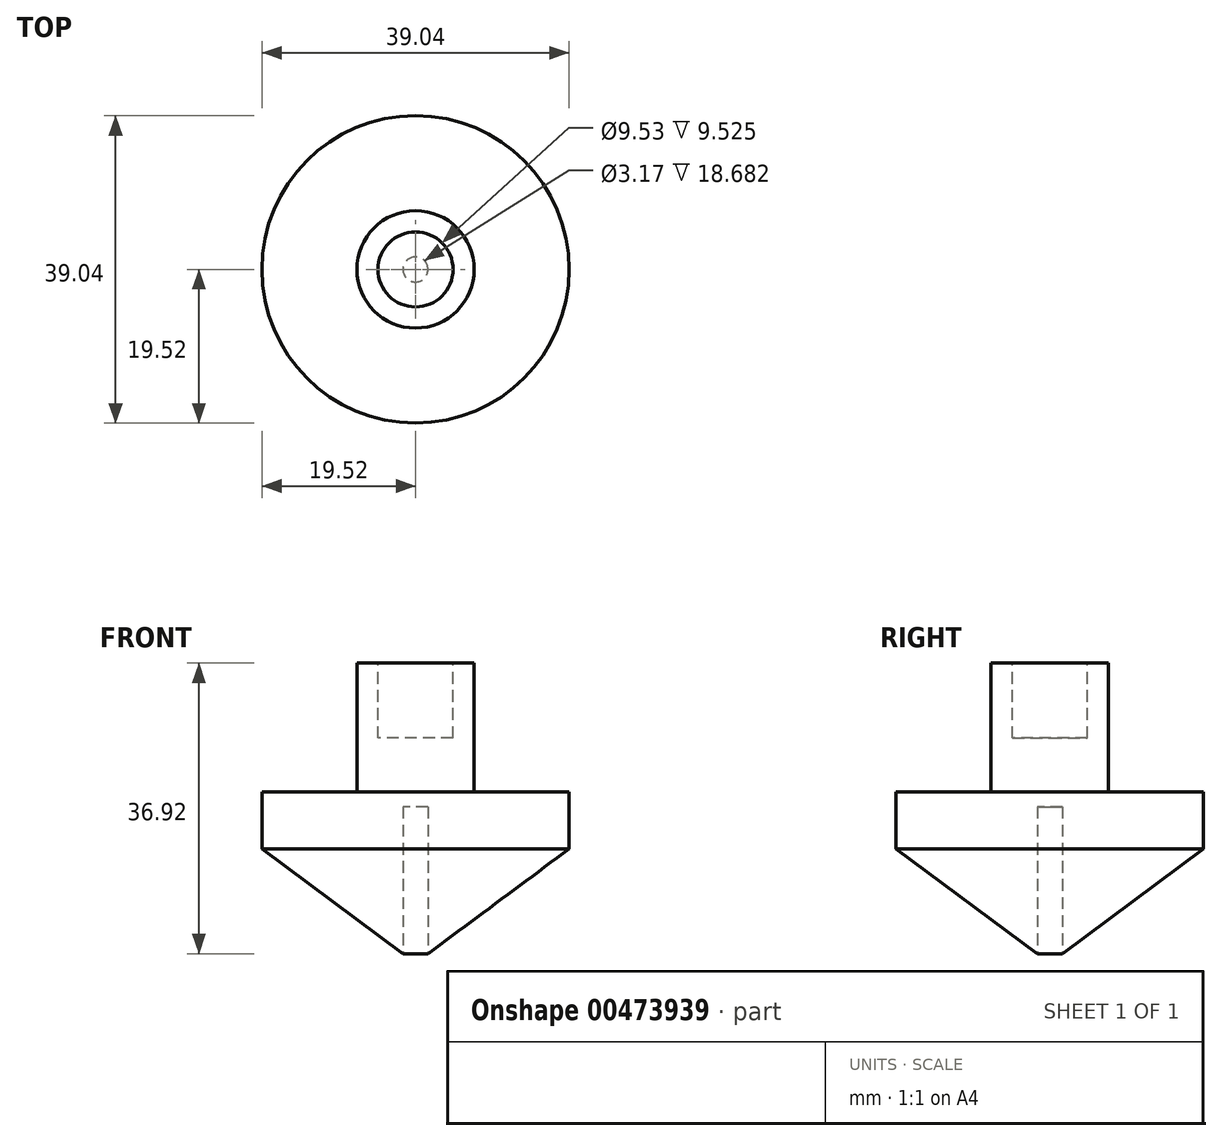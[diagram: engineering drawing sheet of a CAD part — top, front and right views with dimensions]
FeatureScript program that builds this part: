
annotation { "Feature Type Name" : "Feature", "Feature Type Description" : "" }
export const myFeature = defineFeature(function(context is Context, id is Id, definition is map)
    precondition{}
    {
        {
            var Q0;
            Q0=qCreatedBy(makeId("Front.planeOp"),FACE);
            var sketch = newSketch(context, id + "F0", { "sketchPlane" : qUnion([Q0])});
            skLineSegment(sketch, "E0", {"start": v(0, 16.33) * mm, "end": v(7.45, 16.33) * mm});
            skLineSegment(sketch, "E1", {"start": v(7.45, 16.33) * mm, "end": v(7.45, 0) * mm});
            skLineSegment(sketch, "E2", {"start": v(7.45, 0) * mm, "end": v(19.52, 0) * mm});
            skLineSegment(sketch, "E3", {"start": v(19.52, 0) * mm, "end": v(19.52, -7.26) * mm});
            skLineSegment(sketch, "E4", {"start": v(19.52, -7.26) * mm, "end": v(0, -21.77) * mm});
            skLineSegment(sketch, "E5", {"start": v(0, 16.33) * mm, "end": v(0, -21.77) * mm});
            skSolve(sketch);
        }
        {
            var Q0;
            Q0=makeQuery(id+"F0.imprint","IMPRINT",FACE,{"disambiguationData":[TD([[makeQuery(id+"F0.imprint","IMPRINT",EDGE,{"derivedFrom":sQuery(id+"F0.wireOp",EDGE,"E0")}),-1.0]])]});
            var Q1;
            Q1=sQuery(id+"F0.wireOp",EDGE,"E5");
            revolve(context, id + "F1", {"entities" : qUnion([Q0]), "axis" : qUnion([Q1]), "revolveType" : RevolveType.FULL});
        }
        {
            var Q0;
            Q0=makeQuery(id+"F1.opRevolve","SWEPT_FACE",FACE,{"disambiguationData":[OSD([sQuery(id+"F0.wireOp",EDGE,"E0")])]});
            var sketch = newSketch(context, id + "F2", { "sketchPlane" : qUnion([Q0])});
            skCircle(sketch, "E6", {"center": v(0, 0) * mm, "radius": 4.76 * mm});
            skSolve(sketch);
        }
        {
            var Q0;
            Q0=qSketchRegion(id+"F2",true);
            extrude(context, id + "F3", {"entities" : qUnion([Q0]), "operationType" : NewBodyOperationType.REMOVE, "oppositeDirection" : true, "depth" : 9.52 * mm});
        }
        {
            var Q0;
            Q0=qCreatedBy(makeId("Top.planeOp"),FACE);
            cPlane(context, id + "F4", {"entities" : qUnion([Q0]), "cplaneType" : CPlaneType.OFFSET, "offset" : 22.22 * mm, "oppositeDirection" : true, "width" : 152.4 * mm, "height" : 152.4 * mm});
        }
        {
            var Q0;
            Q0=qCreatedBy(id+"F4.planeOp",FACE);
            var sketch = newSketch(context, id + "F5", { "sketchPlane" : qUnion([Q0])});
            skCircle(sketch, "E7", {"center": v(0, 0) * mm, "radius": 1.59 * mm});
            skSolve(sketch);
        }
        {
            var Q0;
            Q0=qSketchRegion(id+"F5",true);
            extrude(context, id + "F6", {"entities" : qUnion([Q0]), "operationType" : NewBodyOperationType.REMOVE, "depth" : 20.32 * mm});
        }
    });
